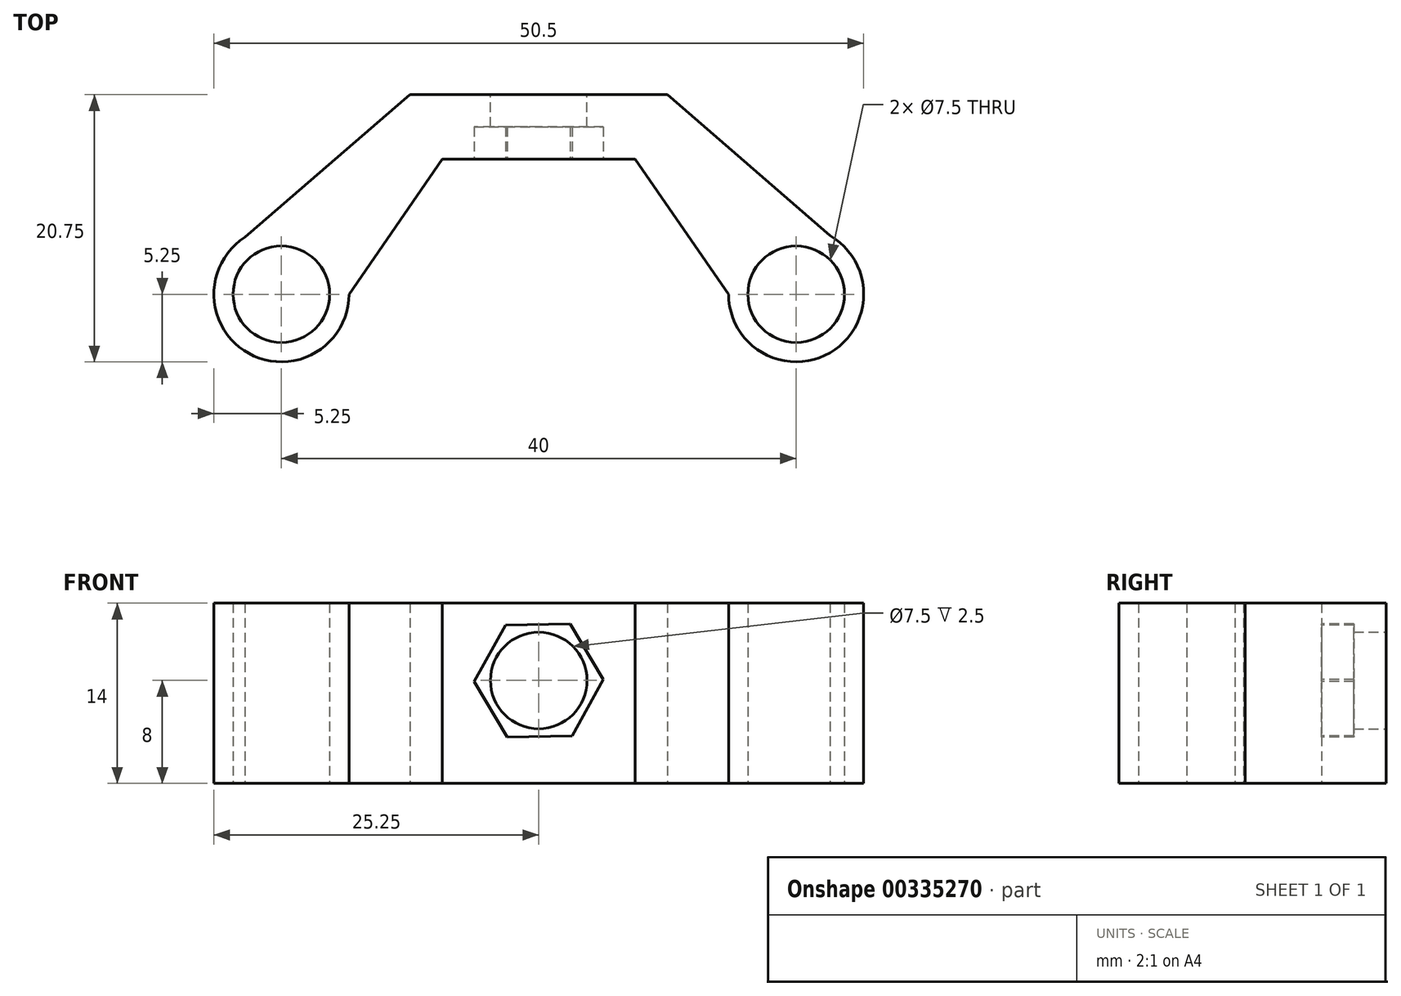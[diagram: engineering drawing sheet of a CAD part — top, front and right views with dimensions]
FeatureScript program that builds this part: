
annotation { "Feature Type Name" : "Feature", "Feature Type Description" : "" }
export const myFeature = defineFeature(function(context is Context, id is Id, definition is map)
    precondition{}
    {
        {
            var Q0;
            Q0=qCreatedBy(makeId("Top.planeOp"),FACE);
            var sketch = newSketch(context, id + "F0", { "sketchPlane" : qUnion([Q0])});
            skCircle(sketch, "E0", {"center": v(-20, 0) * mm, "radius": 3.75 * mm});
            skCircle(sketch, "E1", {"center": v(20, 0) * mm, "radius": 3.75 * mm});
            skSolve(sketch);
        }
        {
            var Q0;
            Q0=qCreatedBy(makeId("Top.planeOp"),FACE);
            var sketch = newSketch(context, id + "F1", { "sketchPlane" : qUnion([Q0])});
            skCircle(sketch, "E2", {"center": v(-20, 0) * mm, "radius": 5.25 * mm});
            skCircle(sketch, "E3", {"center": v(20, 0) * mm, "radius": 5.25 * mm});
            skLineSegment(sketch, "E4", {"start": v(-14.75, 0) * mm, "end": v(-7.5, 10.5) * mm});
            skLineSegment(sketch, "E5", {"start": v(-7.5, 10.5) * mm, "end": v(7.5, 10.5) * mm});
            skLineSegment(sketch, "E6", {"start": v(7.5, 10.5) * mm, "end": v(14.75, 0) * mm});
            skLineSegment(sketch, "E7", {"start": v(-10, 15.5) * mm, "end": v(10, 15.5) * mm});
            skLineSegment(sketch, "E8", {"start": v(-10, 15.5) * mm, "end": v(-22.82, 4.43) * mm});
            skLineSegment(sketch, "E9", {"start": v(10, 15.5) * mm, "end": v(22.63, 4.54) * mm});
            skSolve(sketch);
        }
        {
            var Q0;
            Q0 = qSketchRegion(id + "F0", true);
            extrude(context, id + "F2", {"entities" : qUnion([Q0]), "depth" : 25 * mm});
        }
        {
            var Q0;
            Q0 = qSketchRegion(id + "F1", true);
            extrude(context, id + "F3", {"entities" : qUnion([Q0]), "depth" : 14 * mm});
        }
        {
            var Q0;
            Q0=makeQuery(id+"F3.opExtrude","SWEPT_FACE",FACE,{"disambiguationData":[OSD([sQuery(id+"F1.wireOp",EDGE,"E7")])]});
            var sketch = newSketch(context, id + "F4", { "sketchPlane" : qUnion([Q0])});
            skCircle(sketch, "E10", {"center": v(0, 8) * mm, "radius": 3.75 * mm});
            skSolve(sketch);
        }
        {
            var Q0;
            Q0=makeQuery(id+"F3.opExtrude","SWEPT_FACE",FACE,{"disambiguationData":[OSD([sQuery(id+"F1.wireOp",EDGE,"E5")])]});
            var sketch = newSketch(context, id + "F5", { "sketchPlane" : qUnion([Q0])});
            skCircle(sketch, "E11.cCircle", {"center": v(0, 8) * mm, "radius": 5.02 * mm, "construction": true});
            skLineSegment(sketch, "E11.0", {"start": v(5.02, 8.08) * mm, "end": v(2.58, 3.7) * mm});
            skLineSegment(sketch, "E11.1", {"start": v(2.58, 3.7) * mm, "end": v(-2.44, 3.6) * mm});
            skLineSegment(sketch, "E11.2", {"start": v(-2.44, 3.6) * mm, "end": v(-5.02, 7.92) * mm});
            skLineSegment(sketch, "E11.3", {"start": v(-5.02, 7.92) * mm, "end": v(-2.58, 12.3) * mm});
            skLineSegment(sketch, "E11.4", {"start": v(-2.58, 12.3) * mm, "end": v(2.44, 12.4) * mm});
            skLineSegment(sketch, "E11.5", {"start": v(2.44, 12.4) * mm, "end": v(5.02, 8.08) * mm});
            skSolve(sketch);
        }
        {
            var Q0;
            Q0 = qSketchRegion(id + "F4", true);
            extrude(context, id + "F6", {"entities" : qUnion([Q0]), "oppositeDirection" : true, "depth" : 25 * mm});
        }
        {
            var Q0;
            Q0 = qSketchRegion(id + "F5", true);
            extrude(context, id + "F7", {"entities" : qUnion([Q0]), "oppositeDirection" : true, "depth" : 2.5 * mm});
        }
        {
            var Q0;
            Q0=makeQuery(id+"F2.opExtrude","SWEPT_BODY",BODY,{"disambiguationData":[OSD([sQuery(id+"F0.wireOp",EDGE,"E0")])]});
            var Q1;
            Q1=makeQuery(id+"F2.opExtrude","SWEPT_BODY",BODY,{"disambiguationData":[OSD([sQuery(id+"F0.wireOp",EDGE,"E1")])]});
            var Q2;
            Q2=makeQuery(id+"F6.opExtrude","SWEPT_BODY",BODY,{"disambiguationData":[OSD([sQuery(id+"F4.wireOp",EDGE,"E10")])]});
            var Q3;
            Q3=makeQuery(id+"F7.opExtrude","SWEPT_BODY",BODY,{"disambiguationData":[OSD([sQuery(id+"F5.wireOp",EDGE,"E11.0"),sQuery(id+"F5.wireOp",EDGE,"E11.1"),sQuery(id+"F5.wireOp",EDGE,"E11.2"),sQuery(id+"F5.wireOp",EDGE,"E11.3"),sQuery(id+"F5.wireOp",EDGE,"E11.4"),sQuery(id+"F5.wireOp",EDGE,"E11.5")])]});
            var Q4;
            Q4=makeQuery(id+"F3.opExtrude","SWEPT_BODY",BODY,{"disambiguationData":[OSD([sQuery(id+"F1.wireOp",EDGE,"E2"),sQuery(id+"F1.wireOp",EDGE,"E3"),sQuery(id+"F1.wireOp",EDGE,"E4"),sQuery(id+"F1.wireOp",EDGE,"E5"),sQuery(id+"F1.wireOp",EDGE,"E6"),sQuery(id+"F1.wireOp",EDGE,"E7"),sQuery(id+"F1.wireOp",EDGE,"E8"),sQuery(id+"F1.wireOp",EDGE,"E9")])]});
            booleanBodies(context, id + "F8", {"operationType" : BooleanOperationType.SUBTRACTION, "tools" : qUnion([Q0, Q1, Q2, Q3]), "targets" : qUnion([Q4])});
        }
    });
